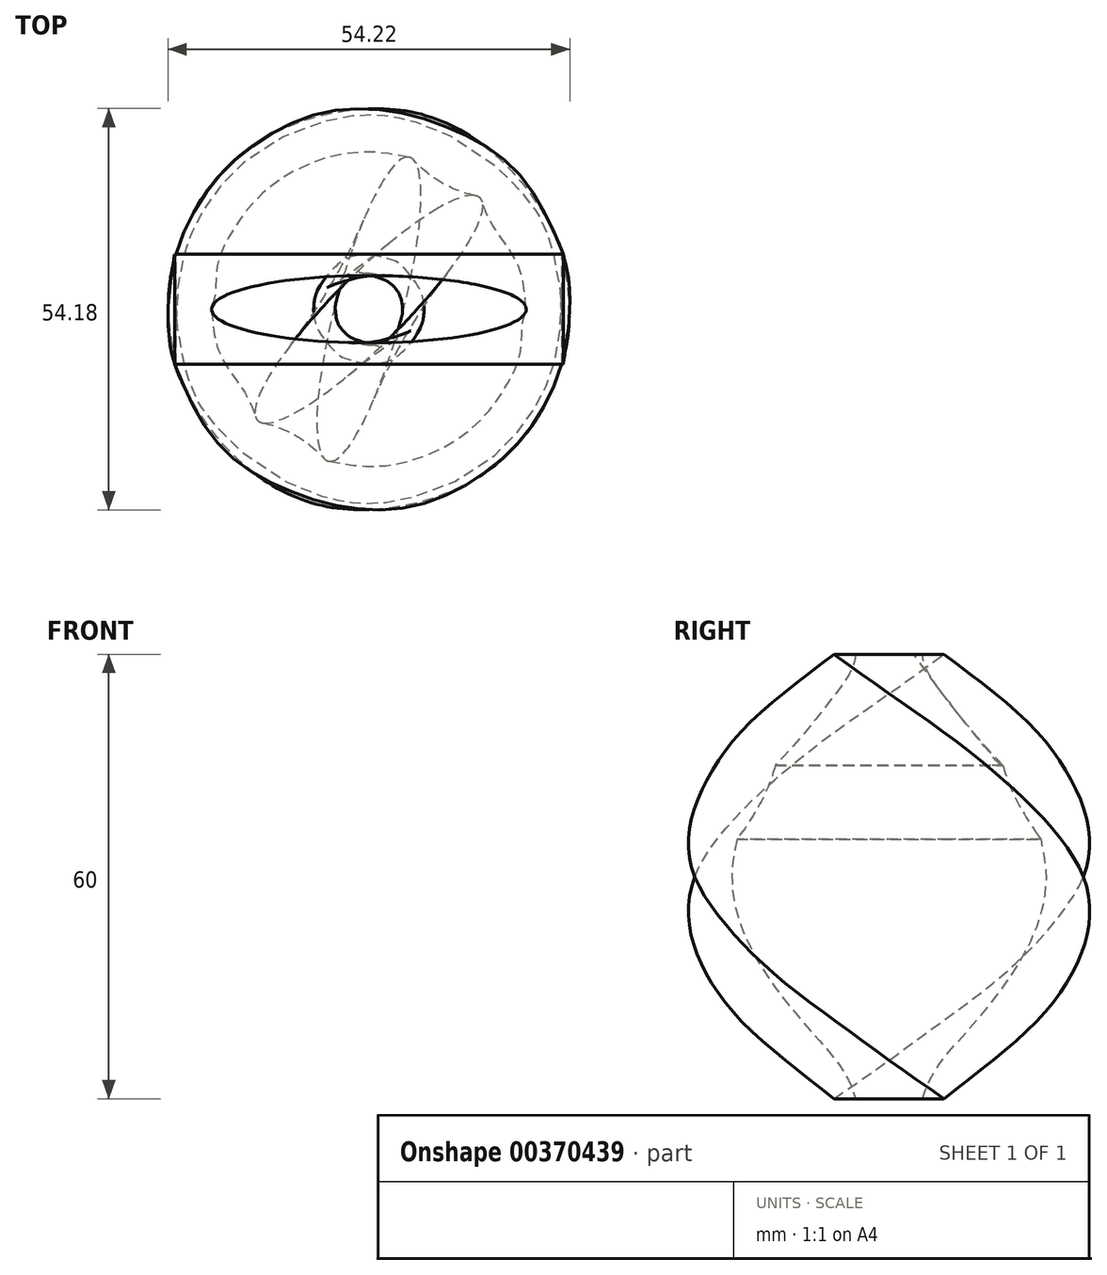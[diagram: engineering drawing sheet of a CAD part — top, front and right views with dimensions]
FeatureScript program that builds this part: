
annotation { "Feature Type Name" : "Feature", "Feature Type Description" : "" }
export const myFeature = defineFeature(function(context is Context, id is Id, definition is map)
    precondition{}
    {
        {
            var Q0;
            Q0=qCreatedBy(makeId("Top.planeOp"),FACE);
            cPlane(context, id + "F0", {"entities" : qUnion([Q0]), "cplaneType" : CPlaneType.OFFSET, "offset" : 5 * mm, "width" : 152.4 * mm, "height" : 152.4 * mm});
        }
        {
            var Q0;
            Q0=qCreatedBy(id+"F0.planeOp",FACE);
            var sketch = newSketch(context, id + "F1", { "sketchPlane" : qUnion([Q0])});
            skLineSegment(sketch, "E0.bottom", {"start": v(-26.04, -7.44) * mm, "end": v(26.04, -7.44) * mm});
            skLineSegment(sketch, "E0.top", {"start": v(-26.04, 7.44) * mm, "end": v(26.04, 7.44) * mm});
            skLineSegment(sketch, "E0.left", {"start": v(-26.04, -7.44) * mm, "end": v(-26.04, 7.44) * mm});
            skLineSegment(sketch, "E0.right", {"start": v(26.04, -7.44) * mm, "end": v(26.04, 7.44) * mm});
            skPoint(sketch, "E0.middle", {"position": v(0, 0) * mm});
            skSolve(sketch);
        }
        {
            var Q0;
            Q0=qCreatedBy(id+"F0.planeOp",FACE);
            var sketch = newSketch(context, id + "F2", { "sketchPlane" : qUnion([Q0])});
            skEllipse(sketch, "E1", {"center": v(0, 0) * mm, "majorRadius": 21.23 * mm, "minorRadius": 4.53 * mm, "majorAxis": v(-1, 0)});
            skSolve(sketch);
        }
        {
            var Q0;
            Q0=qCreatedBy(id+"F0.planeOp",FACE);
            cPlane(context, id + "F3", {"entities" : qUnion([Q0]), "cplaneType" : CPlaneType.OFFSET, "offset" : 5 * mm, "width" : 152.4 * mm, "height" : 152.4 * mm});
        }
        {
            var Q0;
            Q0=qCreatedBy(id+"F3.planeOp",FACE);
            var sketch = newSketch(context, id + "F4", { "sketchPlane" : qUnion([Q0])});
            skLineSegment(sketch, "E2.bottom", {"start": v(-27.03, -0.27) * mm, "end": v(23.27, -13.75) * mm});
            skLineSegment(sketch, "E2.top", {"start": v(-23.27, 13.75) * mm, "end": v(27.03, 0.27) * mm});
            skLineSegment(sketch, "E2.left", {"start": v(-27.03, -0.27) * mm, "end": v(-23.27, 13.75) * mm});
            skLineSegment(sketch, "E2.right", {"start": v(23.27, -13.75) * mm, "end": v(27.03, 0.27) * mm});
            skPoint(sketch, "E2.middle", {"position": v(0, 0) * mm});
            skSolve(sketch);
        }
        {
            var Q0;
            Q0=qCreatedBy(id+"F3.planeOp",FACE);
            var sketch = newSketch(context, id + "F5", { "sketchPlane" : qUnion([Q0])});
            skEllipse(sketch, "E3", {"center": v(0, 0) * mm, "majorRadius": 21.23 * mm, "minorRadius": 4.53 * mm, "majorAxis": v(-0.97, 0.26)});
            skSolve(sketch);
        }
        {
            var Q0;
            Q0=qCreatedBy(id+"F3.planeOp",FACE);
            cPlane(context, id + "F6", {"entities" : qUnion([Q0]), "cplaneType" : CPlaneType.OFFSET, "offset" : 5 * mm, "width" : 152.4 * mm, "height" : 152.4 * mm});
        }
        {
            var Q0;
            Q0=qCreatedBy(id+"F6.planeOp",FACE);
            var sketch = newSketch(context, id + "F7", { "sketchPlane" : qUnion([Q0])});
            skLineSegment(sketch, "E4.bottom", {"start": v(-26.27, 6.58) * mm, "end": v(18.83, -19.46) * mm});
            skLineSegment(sketch, "E4.top", {"start": v(-18.83, 19.46) * mm, "end": v(26.27, -6.58) * mm});
            skLineSegment(sketch, "E4.left", {"start": v(-26.27, 6.58) * mm, "end": v(-18.83, 19.46) * mm});
            skLineSegment(sketch, "E4.right", {"start": v(18.83, -19.46) * mm, "end": v(26.27, -6.58) * mm});
            skPoint(sketch, "E4.middle", {"position": v(0, 0) * mm});
            skSolve(sketch);
        }
        {
            var Q0;
            Q0=qCreatedBy(id+"F6.planeOp",FACE);
            var sketch = newSketch(context, id + "F8", { "sketchPlane" : qUnion([Q0])});
            skEllipse(sketch, "E5", {"center": v(0, 0) * mm, "majorRadius": 21.23 * mm, "minorRadius": 4.53 * mm, "majorAxis": v(-0.87, 0.5)});
            skSolve(sketch);
        }
        {
            var Q0;
            Q0=qCreatedBy(id+"F6.planeOp",FACE);
            cPlane(context, id + "F9", {"entities" : qUnion([Q0]), "cplaneType" : CPlaneType.OFFSET, "offset" : 5 * mm, "width" : 152.4 * mm, "height" : 152.4 * mm});
        }
        {
            var Q0;
            Q0=qCreatedBy(id+"F9.planeOp",FACE);
            var sketch = newSketch(context, id + "F10", { "sketchPlane" : qUnion([Q0])});
            skLineSegment(sketch, "E6.bottom", {"start": v(13.28, -23.54) * mm, "end": v(-23.54, 13.28) * mm});
            skLineSegment(sketch, "E6.top", {"start": v(23.54, -13.28) * mm, "end": v(-13.28, 23.54) * mm});
            skLineSegment(sketch, "E6.left", {"start": v(13.28, -23.54) * mm, "end": v(23.54, -13.28) * mm});
            skLineSegment(sketch, "E6.right", {"start": v(-23.54, 13.28) * mm, "end": v(-13.28, 23.54) * mm});
            skPoint(sketch, "E6.middle", {"position": v(0, 0) * mm});
            skSolve(sketch);
        }
        {
            var Q0;
            Q0=qCreatedBy(id+"F9.planeOp",FACE);
            var sketch = newSketch(context, id + "F11", { "sketchPlane" : qUnion([Q0])});
            skEllipse(sketch, "E7", {"center": v(0, 0) * mm, "majorRadius": 21.23 * mm, "minorRadius": 4.53 * mm, "majorAxis": v(-0.7, 0.7)});
            skSolve(sketch);
        }
        {
            var Q0;
            Q0=qCreatedBy(id+"F9.planeOp",FACE);
            cPlane(context, id + "F12", {"entities" : qUnion([Q0]), "cplaneType" : CPlaneType.OFFSET, "offset" : 5 * mm, "width" : 152.4 * mm, "height" : 152.4 * mm});
        }
        {
            var Q0;
            Q0=qCreatedBy(id+"F12.planeOp",FACE);
            cPlane(context, id + "F13", {"entities" : qUnion([Q0]), "cplaneType" : CPlaneType.OFFSET, "offset" : 5 * mm, "width" : 152.4 * mm, "height" : 152.4 * mm});
        }
        {
            var Q0;
            Q0=qCreatedBy(id+"F13.planeOp",FACE);
            var sketch = newSketch(context, id + "F14", { "sketchPlane" : qUnion([Q0])});
            skLineSegment(sketch, "E8.bottom", {"start": v(-13.92, 23.22) * mm, "end": v(-0.45, -27.07) * mm});
            skLineSegment(sketch, "E8.top", {"start": v(0.45, 27.07) * mm, "end": v(13.92, -23.22) * mm});
            skLineSegment(sketch, "E8.left", {"start": v(-13.92, 23.22) * mm, "end": v(0.45, 27.07) * mm});
            skLineSegment(sketch, "E8.right", {"start": v(-0.45, -27.07) * mm, "end": v(13.92, -23.22) * mm});
            skPoint(sketch, "E8.middle", {"position": v(0, 0) * mm});
            skSolve(sketch);
        }
        {
            var Q0;
            Q0=qCreatedBy(id+"F13.planeOp",FACE);
            var sketch = newSketch(context, id + "F15", { "sketchPlane" : qUnion([Q0])});
            skEllipse(sketch, "E9", {"center": v(0, 0) * mm, "majorRadius": 21.23 * mm, "minorRadius": 4.56 * mm, "majorAxis": v(-0.26, 0.97)});
            skSolve(sketch);
        }
        {
            var Q0;
            Q0=qCreatedBy(id+"F13.planeOp",FACE);
            cPlane(context, id + "F16", {"entities" : qUnion([Q0]), "cplaneType" : CPlaneType.OFFSET, "offset" : 5 * mm, "width" : 152.4 * mm, "height" : 152.4 * mm});
        }
        {
            var Q0;
            Q0=qCreatedBy(id+"F16.planeOp",FACE);
            var sketch = newSketch(context, id + "F17", { "sketchPlane" : qUnion([Q0])});
            skLineSegment(sketch, "E10.bottom", {"start": v(-7.37, 26.24) * mm, "end": v(-7.51, -26.2) * mm});
            skLineSegment(sketch, "E10.top", {"start": v(7.51, 26.2) * mm, "end": v(7.37, -26.24) * mm});
            skLineSegment(sketch, "E10.left", {"start": v(-7.37, 26.24) * mm, "end": v(7.51, 26.2) * mm});
            skLineSegment(sketch, "E10.right", {"start": v(-7.51, -26.2) * mm, "end": v(7.37, -26.24) * mm});
            skPoint(sketch, "E10.middle", {"position": v(0, 0) * mm});
            skSolve(sketch);
        }
        {
            var Q0;
            Q0=qCreatedBy(id+"F16.planeOp",FACE);
            var sketch = newSketch(context, id + "F18", { "sketchPlane" : qUnion([Q0])});
            skEllipse(sketch, "E11", {"center": v(0, 0) * mm, "majorRadius": 21.23 * mm, "minorRadius": 4.53 * mm, "majorAxis": v(0, 1)});
            skSolve(sketch);
        }
        {
            var Q0;
            Q0=qCreatedBy(id+"F16.planeOp",FACE);
            cPlane(context, id + "F19", {"entities" : qUnion([Q0]), "cplaneType" : CPlaneType.OFFSET, "offset" : 5 * mm, "width" : 152.4 * mm, "height" : 152.4 * mm});
        }
        {
            var Q0;
            Q0=qCreatedBy(id+"F19.planeOp",FACE);
            var sketch = newSketch(context, id + "F20", { "sketchPlane" : qUnion([Q0])});
            skLineSegment(sketch, "E12.bottom", {"start": v(-0.45, 27.07) * mm, "end": v(-13.92, -23.22) * mm});
            skLineSegment(sketch, "E12.top", {"start": v(13.92, 23.22) * mm, "end": v(0.45, -27.07) * mm});
            skLineSegment(sketch, "E12.left", {"start": v(-0.45, 27.07) * mm, "end": v(13.92, 23.22) * mm});
            skLineSegment(sketch, "E12.right", {"start": v(-13.92, -23.22) * mm, "end": v(0.45, -27.07) * mm});
            skPoint(sketch, "E12.middle", {"position": v(0, 0) * mm});
            skSolve(sketch);
        }
        {
            var Q0;
            Q0=qCreatedBy(id+"F19.planeOp",FACE);
            var sketch = newSketch(context, id + "F21", { "sketchPlane" : qUnion([Q0])});
            skEllipse(sketch, "E13", {"center": v(0, 0) * mm, "majorRadius": 21.23 * mm, "minorRadius": 4.53 * mm, "majorAxis": v(0.26, 0.97)});
            skSolve(sketch);
        }
        {
            var Q0;
            Q0=qCreatedBy(id+"F19.planeOp",FACE);
            cPlane(context, id + "F22", {"entities" : qUnion([Q0]), "cplaneType" : CPlaneType.OFFSET, "offset" : 5 * mm, "width" : 152.4 * mm, "height" : 152.4 * mm});
        }
        {
            var Q0;
            Q0=qCreatedBy(id+"F22.planeOp",FACE);
            cPlane(context, id + "F23", {"entities" : qUnion([Q0]), "cplaneType" : CPlaneType.OFFSET, "offset" : 5 * mm, "width" : 152.4 * mm, "height" : 152.4 * mm});
        }
        {
            var Q0;
            Q0=qCreatedBy(id+"F23.planeOp",FACE);
            var sketch = newSketch(context, id + "F24", { "sketchPlane" : qUnion([Q0])});
            skLineSegment(sketch, "E14.bottom", {"start": v(13.15, 23.41) * mm, "end": v(-23.41, -13.15) * mm});
            skLineSegment(sketch, "E14.top", {"start": v(23.41, 13.15) * mm, "end": v(-13.15, -23.41) * mm});
            skLineSegment(sketch, "E14.left", {"start": v(13.15, 23.41) * mm, "end": v(23.41, 13.15) * mm});
            skLineSegment(sketch, "E14.right", {"start": v(-23.41, -13.15) * mm, "end": v(-13.15, -23.41) * mm});
            skPoint(sketch, "E14.middle", {"position": v(0, 0) * mm});
            skSolve(sketch);
        }
        {
            var Q0;
            Q0=qCreatedBy(id+"F23.planeOp",FACE);
            var sketch = newSketch(context, id + "F25", { "sketchPlane" : qUnion([Q0])});
            skEllipse(sketch, "E15", {"center": v(0, 0) * mm, "majorRadius": 21.23 * mm, "minorRadius": 4.72 * mm, "majorAxis": v(0.7, 0.7)});
            skSolve(sketch);
        }
        {
            var Q0;
            Q0=qCreatedBy(id+"F23.planeOp",FACE);
            cPlane(context, id + "F26", {"entities" : qUnion([Q0]), "cplaneType" : CPlaneType.OFFSET, "offset" : 5 * mm, "width" : 152.4 * mm, "height" : 152.4 * mm});
        }
        {
            var Q0;
            Q0=qCreatedBy(id+"F26.planeOp",FACE);
            var sketch = newSketch(context, id + "F27", { "sketchPlane" : qUnion([Q0])});
            skLineSegment(sketch, "E16.bottom", {"start": v(18.98, 19.55) * mm, "end": v(-26.42, -6.67) * mm});
            skLineSegment(sketch, "E16.top", {"start": v(26.42, 6.67) * mm, "end": v(-18.98, -19.55) * mm});
            skLineSegment(sketch, "E16.left", {"start": v(18.98, 19.55) * mm, "end": v(26.42, 6.67) * mm});
            skLineSegment(sketch, "E16.right", {"start": v(-26.42, -6.67) * mm, "end": v(-18.98, -19.55) * mm});
            skPoint(sketch, "E16.middle", {"position": v(0, 0) * mm});
            skSolve(sketch);
        }
        {
            var Q0;
            Q0=qCreatedBy(id+"F26.planeOp",FACE);
            cPlane(context, id + "F28", {"entities" : qUnion([Q0]), "cplaneType" : CPlaneType.OFFSET, "offset" : 5 * mm, "width" : 152.4 * mm, "height" : 152.4 * mm});
        }
        {
            var Q0;
            Q0=qCreatedBy(id+"F28.planeOp",FACE);
            var sketch = newSketch(context, id + "F29", { "sketchPlane" : qUnion([Q0])});
            skLineSegment(sketch, "E17.bottom", {"start": v(23.22, 13.92) * mm, "end": v(-27.07, 0.45) * mm});
            skLineSegment(sketch, "E17.top", {"start": v(27.07, -0.45) * mm, "end": v(-23.22, -13.92) * mm});
            skLineSegment(sketch, "E17.left", {"start": v(23.22, 13.92) * mm, "end": v(27.07, -0.45) * mm});
            skLineSegment(sketch, "E17.right", {"start": v(-27.07, 0.45) * mm, "end": v(-23.22, -13.92) * mm});
            skPoint(sketch, "E17.middle", {"position": v(0, 0) * mm});
            skSolve(sketch);
        }
        {
            var Q0;
            Q0=qCreatedBy(id+"F28.planeOp",FACE);
            var sketch = newSketch(context, id + "F30", { "sketchPlane" : qUnion([Q0])});
            skEllipse(sketch, "E18", {"center": v(0, 0) * mm, "majorRadius": 21.04 * mm, "minorRadius": 4.53 * mm, "majorAxis": v(0.97, 0.26)});
            skSolve(sketch);
        }
        {
            var Q0;
            Q0=qCreatedBy(id+"F28.planeOp",FACE);
            cPlane(context, id + "F31", {"entities" : qUnion([Q0]), "cplaneType" : CPlaneType.OFFSET, "offset" : 5 * mm, "width" : 152.4 * mm, "height" : 152.4 * mm});
        }
        {
            var Q0;
            Q0=qCreatedBy(id+"F31.planeOp",FACE);
            var sketch = newSketch(context, id + "F32", { "sketchPlane" : qUnion([Q0])});
            skLineSegment(sketch, "E19.bottom", {"start": v(26.22, 7.44) * mm, "end": v(-26.22, 7.44) * mm});
            skLineSegment(sketch, "E19.top", {"start": v(26.22, -7.44) * mm, "end": v(-26.22, -7.44) * mm});
            skLineSegment(sketch, "E19.left", {"start": v(26.22, 7.44) * mm, "end": v(26.22, -7.44) * mm});
            skLineSegment(sketch, "E19.right", {"start": v(-26.22, 7.44) * mm, "end": v(-26.22, -7.44) * mm});
            skPoint(sketch, "E19.middle", {"position": v(0, 0) * mm});
            skSolve(sketch);
        }
        {
            var Q0;
            Q0=qCreatedBy(id+"F31.planeOp",FACE);
            var sketch = newSketch(context, id + "F33", { "sketchPlane" : qUnion([Q0])});
            skEllipse(sketch, "E20", {"center": v(0, 0) * mm, "majorRadius": 21.23 * mm, "minorRadius": 4.54 * mm, "majorAxis": v(-1, 0)});
            skSolve(sketch);
        }
        {
            var Q0;
            Q0 = qSketchRegion(id + "F1", true);
            var Q1;
            Q1 = qSketchRegion(id + "F4", true);
            var Q2;
            Q2 = qSketchRegion(id + "F7", true);
            var Q3;
            Q3 = qSketchRegion(id + "F10", true);
            var Q4;
            Q4 = qSketchRegion(id + "F14", true);
            var Q5;
            Q5 = qSketchRegion(id + "F17", true);
            var Q6;
            Q6 = qSketchRegion(id + "F20", true);
            var Q7;
            Q7 = qSketchRegion(id + "F24", true);
            var Q8;
            Q8 = qSketchRegion(id + "F27", true);
            var Q9;
            Q9 = qSketchRegion(id + "F29", true);
            var Q10;
            Q10 = qSketchRegion(id + "F32", true);
            loft(context, id + "F34", {"sheetProfilesArray" : [{ "sheetProfileEntities" : qUnion([Q0]) }, { "sheetProfileEntities" : qUnion([Q1]) }, { "sheetProfileEntities" : qUnion([Q2]) }, { "sheetProfileEntities" : qUnion([Q3]) }, { "sheetProfileEntities" : qUnion([Q4]) }, { "sheetProfileEntities" : qUnion([Q5]) }, { "sheetProfileEntities" : qUnion([Q6]) }, { "sheetProfileEntities" : qUnion([Q7]) }, { "sheetProfileEntities" : qUnion([Q8]) }, { "sheetProfileEntities" : qUnion([Q9]) }, { "sheetProfileEntities" : qUnion([Q10]) }]});
        }
        {
            var Q1;
            Q1 = qSketchRegion(id + "F2", true);
            var Q2;
            Q2 = qSketchRegion(id + "F5", true);
            var Q3;
            Q3 = qSketchRegion(id + "F8", true);
            var Q4;
            Q4 = qSketchRegion(id + "F11", true);
            var Q5;
            Q5 = qSketchRegion(id + "F15", true);
            var Q6;
            Q6 = qSketchRegion(id + "F18", true);
            var Q7;
            Q7 = qSketchRegion(id + "F21", true);
            loft(context, id + "F35", {"operationType" : NewBodyOperationType.REMOVE, "sheetProfilesArray" : [{ "sheetProfileEntities" : qUnion([Q1]) }, { "sheetProfileEntities" : qUnion([Q2]) }, { "sheetProfileEntities" : qUnion([Q3]) }, { "sheetProfileEntities" : qUnion([Q4]) }, { "sheetProfileEntities" : qUnion([Q5]) }, { "sheetProfileEntities" : qUnion([Q6]) }, { "sheetProfileEntities" : qUnion([Q7]) }]});
        }
        {
            var Q1;
            Q1 = qSketchRegion(id + "F25", true);
            var Q2;
            Q2 = qSketchRegion(id + "F30", true);
            var Q3;
            Q3 = qSketchRegion(id + "F33", true);
            loft(context, id + "F36", {"operationType" : NewBodyOperationType.REMOVE, "sheetProfilesArray" : [{ "sheetProfileEntities" : qUnion([Q1]) }, { "sheetProfileEntities" : qUnion([Q2]) }, { "sheetProfileEntities" : qUnion([Q3]) }]});
        }
        {
            var Q1;
            Q1 = qSketchRegion(id + "F21", true);
            var Q2;
            Q2 = qSketchRegion(id + "F25", true);
            loft(context, id + "F37", {"operationType" : NewBodyOperationType.REMOVE, "sheetProfilesArray" : [{ "sheetProfileEntities" : qUnion([Q1]) }, { "sheetProfileEntities" : qUnion([Q2]) }]});
        }
    });
